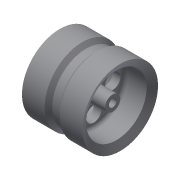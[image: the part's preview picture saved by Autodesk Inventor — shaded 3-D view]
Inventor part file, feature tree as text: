
AUTODESK INVENTOR PART (.ipt)
format: ipt  version: 2015 (Build 190159000, 159)  size: 180,224 bytes
history: native  units: mm
features: sketch x5, hole x3, revolve x1
ambient origin geometry x8: Origin, YZ Plane, XZ Plane, XY Plane, X Axis, Y Axis, Z Axis, Center Point
bodies: Solid1 (feature_tree)
feature tree (9):
  revolve  "Revolution1"  [1 undecoded]
  hole  "Hole1"  [1 undecoded]
  hole  "Hole2"  [1 undecoded]
  sketch  "Sketch4"  dims[d14=90.0deg d15=3.0mm]
  hole  "Hole3"  [1 undecoded]
  sketch  "Sketch1"  dims[d0=6.0mm d1=2.0mm]
  sketch  "Sketch2"  dims[d3=5.0mm d6=12.0mm]
  sketch  "Sketch3"  dims[d7=2.0mm d8=5.0mm]
  sketch  "Sketch5"  dims[d16=3.0mm d17=3.0mm d18=3.0mm d19=5.0mm d20=6.0mm d21=4.0mm d22=2.0mm d23=90.0deg d24=8.0mm d25=0.0mm d26=5.0mm d27=5.0mm d28=6.0mm d29=5.0mm d30=5.0mm d31=3.0mm d32=3.0mm d33=3.0mm d34=3.0mm d35=4.0mm d36=6.0mm d37=4.0mm d38=2.0mm d39=90.0deg d40=8.0mm d41=0.0mm d42=2.0mm d43=6.0mm d44=4.0mm d45=2.0mm d46=90.0deg d47=20.0mm d48=0.0mm]
note: 4 required parameter values undecoded (feature->parameter linkage not recoverable at this tier; creation-order binding heuristic only, values carry confidence <= 0.55)